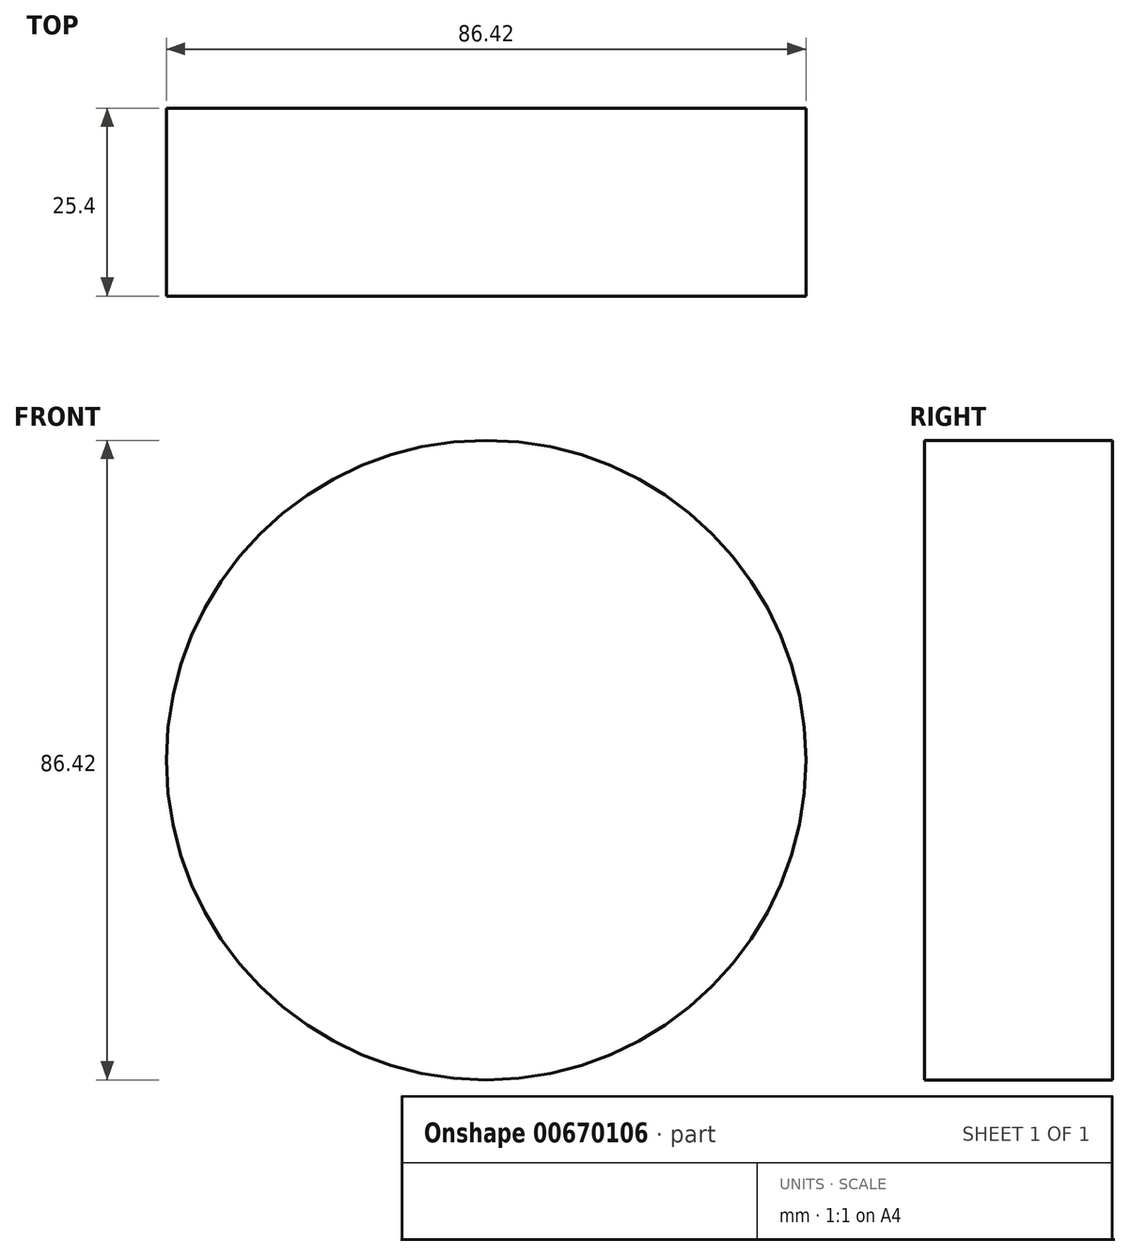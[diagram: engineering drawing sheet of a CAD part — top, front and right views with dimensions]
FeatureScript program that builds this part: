
annotation { "Feature Type Name" : "Feature", "Feature Type Description" : "" }
export const myFeature = defineFeature(function(context is Context, id is Id, definition is map)
    precondition{}
    {
        {
            var Q0;
            Q0=qCreatedBy(makeId("Front.planeOp"),FACE);
            var sketch = newSketch(context, id + "F0", { "sketchPlane" : qUnion([Q0])});
            skCircle(sketch, "E0", {"center": v(0, 0) * mm, "radius": 43.2 * mm});
            skSolve(sketch);
        }
        {
            var Q0;
            Q0 = qSketchRegion(id + "F0", true);
            extrude(context, id + "F1", {"entities" : qUnion([Q0]), "depth" : 25.4 * mm, "offsetDistance" : 25.4 * mm});
        }
    });
